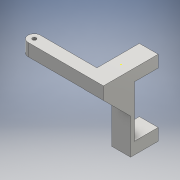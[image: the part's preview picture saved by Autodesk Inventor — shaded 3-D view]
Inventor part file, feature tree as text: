
AUTODESK INVENTOR PART (.ipt)
format: ipt  version: 2016 (Build 200138000, 138)  size: 145,408 bytes
history: native  units: mm
features: sketch x7, extrude x5, fillet x1, hole x1
ambient origin geometry x8: Origin, YZ Plane, XZ Plane, XY Plane, X Axis, Y Axis, Z Axis, Center Point
bodies: Solid1 (feature_tree)
feature tree (14):
  extrude  "Extrusion1"  Depth=60.0mm
  extrude  "Extrusion2"  Depth=41.0mm
  extrude  "Extrusion3"  Depth=10.0mm
  extrude  "Extrusion5"  Depth=15.0mm TaperAngle=0.0deg
  extrude  "Extrusion6"  Depth=15.0mm TaperAngle=0.0deg
  sketch  "Sketch7"  dims[d19=50.0mm d20=0.0mm d21=5.0mm]
  fillet  "Fillet1"  Radius=9.871mm
  hole  "Hole1"  [1 undecoded]
  sketch  "Sketch1"  dims[d0=15.0mm d1=60.0mm]
  sketch  "Sketch2"  dims[d2=3.0mm d3=0.0mm d4=41.0mm]
  sketch  "Sketch3"  dims[d5=19.0mm d6=0.0mm d7=10.0mm]
  sketch  "Sketch5"  dims[d8=21.64mm d9=15.0mm d10=0.0mm]
  sketch  "Sketch6"  dims[d15=45.0deg d16=15.0mm d17=0.0mm d18=9.871mm]
  sketch  "Sketch8"  dims[d22=3.0mm d23=6.0mm d24=4.0mm d25=2.0mm d26=90.0deg d27=8.0mm d28=20.594885mm]
note: 1 required parameter value undecoded (feature->parameter linkage not recoverable at this tier; creation-order binding heuristic only, values carry confidence <= 0.55)
